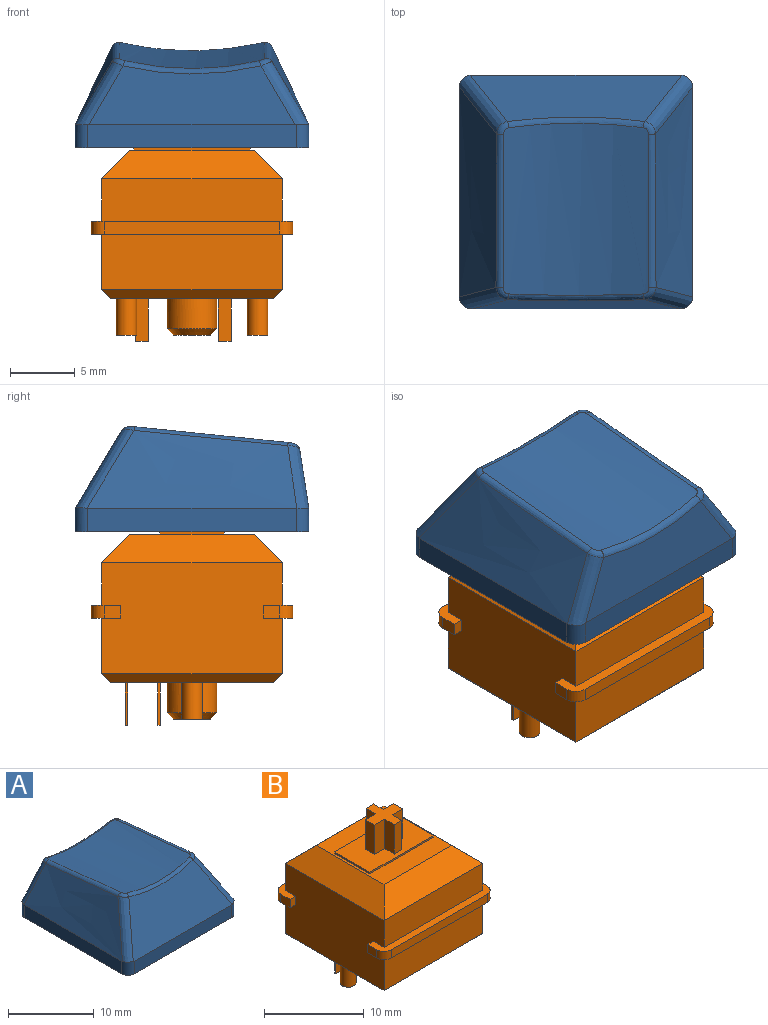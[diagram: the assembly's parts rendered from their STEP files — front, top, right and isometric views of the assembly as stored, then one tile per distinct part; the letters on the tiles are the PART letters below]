
ASSEMBLY  parts=2 mates=1
PART A: 50 faces, bbox 21.2x21.9x10.6 mm
  f0: plane 18.1x18.1mm, normal (0,0,-1), area 67.5mm2, adj f1,f2,f3,f4,f10,f12,f14,f16
  f1: plane 16.1x1.8mm, normal (1,0,0), area 29mm2, adj f0,f8,f10,f16
  f2: plane 16.1x1.8mm, normal (0,1,0), area 29mm2, adj f0,f5,f14,f15,f16,f17
  f3: plane 16.1x1.8mm, normal (-1,0,0), area 29mm2, adj f0,f6,f12,f14
  f4: plane 16.1x1.8mm, normal (0,-1,0), area 29mm2, adj f0,f7,f10,f12
  f5: plane 15.96x4.53mm, normal (0,0.99,0.15), area 56.4mm2, adj f2,f15,f17,f20
  f6: bspline ~18.1x6.49mm, area 87.4mm2, adj f3,f12,f13,f14,f15,f19
  f7: plane 16.37x6.05mm, normal (0,-0.86,0.51), area 90.2mm2, adj f4,f10,f11,f12,f13,f23
  f8: bspline ~18.1x6.49mm, area 87.4mm2, adj f1,f10,f11,f16,f17,f24
  f9: cylinder r=22.9mm len=12.94mm, axis (0,0.99,-0.1), area 146.4mm2, adj f18,f19,f20,f21,f22,f23,f24,f25
  f10: cylinder r=1mm len=1.88mm, axis (0,0,-1), area 2.9mm2, adj f0,f1,f4,f7,f8,f11
  f11: bspline ~7.99x5.46mm, area 10.4mm2, adj f7,f8,f10,f25
  f12: cylinder r=1mm len=1.88mm, axis (0,0,1), area 2.9mm2, adj f0,f3,f4,f6,f7,f13
  f13: bspline ~8.01x5.47mm, area 10.4mm2, adj f6,f7,f12,f21
  f14: cylinder r=1mm len=1.8mm, axis (0,0,-1), area 2.8mm2, adj f0,f2,f3,f6,f15
  f15: bspline ~6.46x4.4mm, area 8.2mm2, adj f2,f5,f6,f14,f18
  f16: cylinder r=1mm len=1.8mm, axis (0,0,1), area 2.8mm2, adj f0,f1,f2,f8,f17
  f17: bspline ~6.45x4.39mm, area 8.2mm2, adj f2,f5,f8,f16,f22
  f18: bspline ~1.17x1.02mm, area 0.7mm2, adj f9,f15,f19,f20
  f19: bspline ~17.37x2.1mm, area 8mm2, adj f6,f9,f18,f21
  f20: bspline ~10.64x1.03mm, area 7mm2, adj f5,f9,f18,f22
  f21: bspline ~1.13x1.07mm, area 0.7mm2, adj f9,f13,f19,f23
  f22: bspline ~1.17x1mm, area 0.7mm2, adj f9,f17,f20,f24
  f23: bspline ~10.62x0.82mm, area 6mm2, adj f7,f9,f21,f25
  f24: bspline ~17.37x2.1mm, area 8mm2, adj f8,f9,f22,f25
  f25: bspline ~1.24x1.01mm, area 0.7mm2, adj f9,f11,f23,f24
  f26: plane 16.13x1.61mm, normal (-1,0,0), area 25mm2, adj f0,f27,f29,f32,f33
  f27: plane 16.1x1.72mm, normal (0,-1,0), area 27.7mm2, adj f0,f26,f28,f30,f31,f33
  f28: plane 16.13x1.61mm, normal (1,0,0), area 25mm2, adj f0,f27,f29,f31,f32
  f29: plane 16.1x1.52mm, normal (0,1,0), area 24.5mm2, adj f0,f26,f28,f32
  f30: plane 16.21x4.45mm, normal (0,-0.99,-0.15), area 51mm2, adj f27,f31,f33,f34
  f31: offset ~20.1x8.49mm, area 78.8mm2, adj f27,f28,f30,f32,f34
  f32: plane 16.68x6.12mm, normal (0,0.86,-0.51), area 82.2mm2, adj f26,f28,f29,f31,f33,f34
  f33: offset ~20.1x8.49mm, area 78.8mm2, adj f26,f27,f30,f32,f34
  f34: cylinder r=23.9mm len=12.22mm, axis (0,0.99,-0.1), area 111.1mm2, adj f30,f31,f32,f33,f46
  f35: plane 5.88x1.35mm, normal (-1,0,0), area 7.8mm2, adj f36,f44,f45,f49
  f36: plane 5.97x1.5mm, normal (0,-1,0), area 8.9mm2, adj f35,f37,f45,f49
  f37: plane 6.1x1.3mm, normal (-1,0,0), area 7.8mm2, adj f36,f38,f45,f49
  f38: plane 6.1x1.5mm, normal (0,1,0), area 9.1mm2, adj f37,f39,f45,f49
  f39: plane 6.16x1.35mm, normal (-1,0,0), area 8.2mm2, adj f38,f40,f45,f49
  f40: plane 6.16x1mm, normal (0,1,0), area 6.2mm2, adj f39,f41,f45,f49
  f41: plane 6.16x1.35mm, normal (1,0,0), area 8.2mm2, adj f40,f42,f45,f49
  f42: plane 6.1x1.5mm, normal (0,1,0), area 9.1mm2, adj f41,f43,f45,f49
  f43: plane 6.1x1.3mm, normal (1,0,0), area 7.8mm2, adj f42,f45,f47,f49
  f44: plane 5.74x1mm, normal (0,-1,0), area 5.7mm2, adj f35,f45,f48,f49
  f45: plane 5.5x5.5mm, normal (0,0,-1), area 15.9mm2, adj f35,f36,f37,f38,f39,f40,f41,f42
  f46: cylinder r=2.75mm len=6.11mm, axis (0,0,-1), area 105.5mm2, adj f34,f45
  f47: plane 5.97x1.5mm, normal (0,-1,0), area 8.9mm2, adj f43,f45,f48,f49
  f48: plane 5.88x1.35mm, normal (1,0,0), area 7.8mm2, adj f44,f45,f47,f49
  f49: cylinder r=23.9mm len=4.01mm, axis (0,0.99,-0.1), area 7.9mm2, adj f35,f36,f37,f38,f39,f40,f41,f42
PART B: 69 faces, bbox 15.6x15.6x18.6 mm
  f0: plane 15.6x2.3mm, normal (0,0,-1), area 14.4mm2, adj f2,f3,f28,f30,f35,f60,f62,f63
  f1: plane 15.6x2.3mm, normal (0,0,-1), area 14.4mm2, adj f28,f30,f33,f34,f36,f59,f61,f64
  f2: plane 1.3x1mm, normal (1,0,0), area 1.3mm2, adj f0,f32,f62,f66
  f3: plane 1.3x1mm, normal (-1,0,0), area 1.3mm2, adj f0,f32,f63,f68
  f4: plane 15.6x2.3mm, normal (0,0,1), area 14.4mm2, adj f28,f30,f31,f33,f34,f36,f61,f64
  f5: plane 14x2.2mm, normal (-0.71,0,0.71), area 36.7mm2, adj f6,f7,f26,f30
  f6: plane 14x2.2mm, normal (0,-0.71,0.71), area 36.7mm2, adj f5,f7,f27,f31
  f7: plane 9.6x9.6mm, normal (0,0,1), area 47.2mm2, adj f5,f6,f8,f9,f10,f11,f26,f27
  f8: plane 5x0.2mm, normal (1,0,0), area 1mm2, adj f7,f9,f11,f12
  f9: plane 9x0.2mm, normal (0,1,0), area 1.8mm2, adj f7,f8,f10,f12
  f10: plane 5x0.2mm, normal (-1,0,0), area 1mm2, adj f7,f9,f11,f12
  f11: plane 9x0.2mm, normal (0,-1,0), area 1.8mm2, adj f7,f8,f10,f12
  f12: plane 9x5mm, normal (0,0,1), area 36.9mm2, adj f8,f9,f10,f11,f13,f14,f15,f16
  f13: plane 3.6x1.35mm, normal (1,0,0), area 4.9mm2, adj f12,f14,f24,f25
  f14: plane 3.6x1.08mm, normal (0,1,0), area 3.9mm2, adj f12,f13,f15,f25
  f15: plane 3.6x1.35mm, normal (-1,0,0), area 4.9mm2, adj f12,f14,f16,f25
  f16: plane 3.6x1.46mm, normal (0,1,0), area 5.3mm2, adj f12,f15,f17,f25
  f17: plane 3.6x1.3mm, normal (-1,0,0), area 4.7mm2, adj f12,f16,f18,f25
  f18: plane 3.6x1.46mm, normal (0,-1,0), area 5.3mm2, adj f12,f17,f19,f25
  f19: plane 3.6x1.35mm, normal (-1,0,0), area 4.9mm2, adj f12,f18,f20,f25
  f20: plane 3.6x1.08mm, normal (0,-1,0), area 3.9mm2, adj f12,f19,f21,f25
  f21: plane 3.6x1.35mm, normal (1,0,0), area 4.9mm2, adj f12,f20,f22,f25
  f22: plane 3.6x1.46mm, normal (0,-1,0), area 5.3mm2, adj f12,f21,f23,f25
  f23: plane 3.6x1.3mm, normal (1,0,0), area 4.7mm2, adj f12,f22,f24,f25
  f24: plane 3.6x1.46mm, normal (0,1,0), area 5.3mm2, adj f12,f13,f23,f25
  f25: plane 4x4mm, normal (0,0,1), area 8.1mm2, adj f13,f14,f15,f16,f17,f18,f19,f20
  f26: plane 14x2.2mm, normal (0,0.71,0.71), area 36.7mm2, adj f5,f7,f27,f29
  f27: plane 14x2.2mm, normal (0.71,0,0.71), area 36.7mm2, adj f6,f7,f26,f28
  f28: plane 14x8.6mm, normal (1,0,0), area 117.4mm2, adj f0,f1,f4,f27,f29,f31,f32,f55
  f29: plane 14x3.3mm, normal (0,1,0), area 46.2mm2, adj f26,f28,f30,f32
  f30: plane 14x8.6mm, normal (-1,0,0), area 117.4mm2, adj f0,f1,f4,f5,f29,f31,f32,f57
  f31: plane 14x3.3mm, normal (0,-1,0), area 46.2mm2, adj f4,f6,f28,f30
  f32: plane 15.6x2.3mm, normal (0,0,1), area 14.4mm2, adj f2,f3,f28,f29,f30,f35,f62,f63
  f33: plane 13.6x1mm, normal (0,-1,0), area 13.6mm2, adj f1,f4,f61,f64
  f34: plane 1.3x1mm, normal (1,0,0), area 1.3mm2, adj f1,f4,f61,f65
  f35: plane 13.6x1mm, normal (0,1,0), area 13.6mm2, adj f0,f32,f62,f63
  f36: plane 1.3x1mm, normal (-1,0,0), area 1.3mm2, adj f1,f4,f64,f67
  f37: plane 2.85x2.85mm, normal (0,0,-1), area 6.4mm2, adj f38
  f38: cone r=1.43mm half-angle=45deg, axis (0,0,1), area 7.4mm2, adj f37,f43
  f39: plane 1x0.2mm, normal (0,0,-1), area 0.2mm2, adj f44,f45,f46,f47
  f40: plane 1x0.2mm, normal (0,0,-1), area 0.2mm2, adj f48,f49,f50,f51
  f41: plane 1.6x1.6mm, normal (0,0,-1), area 2mm2, adj f52
  f42: plane 1.6x1.6mm, normal (0,0,-1), area 2mm2, adj f53
  f43: cylinder r=1.93mm len=3.85mm, axis (0,0,1), area 27.8mm2, adj f38,f54
  f44: plane 3.3x0.2mm, normal (-1,0,0), area 0.7mm2, adj f39,f45,f47,f54
  f45: plane 3.3x1mm, normal (0,1,0), area 3.3mm2, adj f39,f44,f46,f54
  f46: plane 3.3x0.2mm, normal (1,0,0), area 0.7mm2, adj f39,f45,f47,f54
  f47: plane 3.3x1mm, normal (0,-1,0), area 3.3mm2, adj f39,f44,f46,f54
  f48: plane 3.3x0.2mm, normal (-1,0,0), area 0.7mm2, adj f40,f49,f51,f54
  f49: plane 3.3x1mm, normal (0,1,0), area 3.3mm2, adj f40,f48,f50,f54
  f50: plane 3.3x0.2mm, normal (1,0,0), area 0.7mm2, adj f40,f49,f51,f54
  f51: plane 3.3x1mm, normal (0,-1,0), area 3.3mm2, adj f40,f48,f50,f54
  f52: cylinder r=0.8mm len=2.8mm, axis (0,0,1), area 14.1mm2, adj f41,f54
  f53: cylinder r=0.8mm len=2.8mm, axis (0,0,1), area 14.1mm2, adj f42,f54
  f54: plane 12.6x12.6mm, normal (0,0,-1), area 142.7mm2, adj f43,f44,f45,f46,f47,f48,f49,f50
  f55: plane 14x0.7mm, normal (0.71,0,-0.71), area 13.2mm2, adj f28,f54,f56,f58
  f56: plane 14x0.7mm, normal (0,0.71,-0.71), area 13.2mm2, adj f54,f55,f57,f60
  f57: plane 14x0.7mm, normal (-0.71,0,-0.71), area 13.2mm2, adj f30,f54,f56,f58
  f58: plane 14x0.7mm, normal (0,-0.71,-0.71), area 13.2mm2, adj f54,f55,f57,f59
  f59: plane 14x4.3mm, normal (0,-1,0), area 60.2mm2, adj f1,f28,f30,f58
  f60: plane 14x4.3mm, normal (0,1,0), area 60.2mm2, adj f0,f28,f30,f56
  f61: cylinder r=1mm len=1mm, axis (0,0,-1), area 1.6mm2, adj f1,f4,f33,f34
  f62: cylinder r=1mm len=1mm, axis (0,0,1), area 1.6mm2, adj f0,f2,f32,f35
  f63: cylinder r=1mm len=1mm, axis (0,0,-1), area 1.6mm2, adj f0,f3,f32,f35
  f64: cylinder r=1mm len=1mm, axis (0,0,1), area 1.6mm2, adj f1,f4,f33,f36
  f65: plane 1x0.8mm, normal (0,1,0), area 0.8mm2, adj f1,f4,f28,f34
  f66: plane 1x0.8mm, normal (0,-1,0), area 0.8mm2, adj f0,f2,f28,f32
  f67: plane 1x0.8mm, normal (0,1,0), area 0.8mm2, adj f1,f4,f30,f36
  f68: plane 1x0.8mm, normal (0,-1,0), area 0.8mm2, adj f0,f3,f30,f32
PLACE A rot(axis=(0,0,1),180deg) t=(0,0,11.7)mm
PLACE B at identity fixed
MATE fastened B.f38 <-> A.f46  axis (0,0,1) through (0,0,11.7)mm
